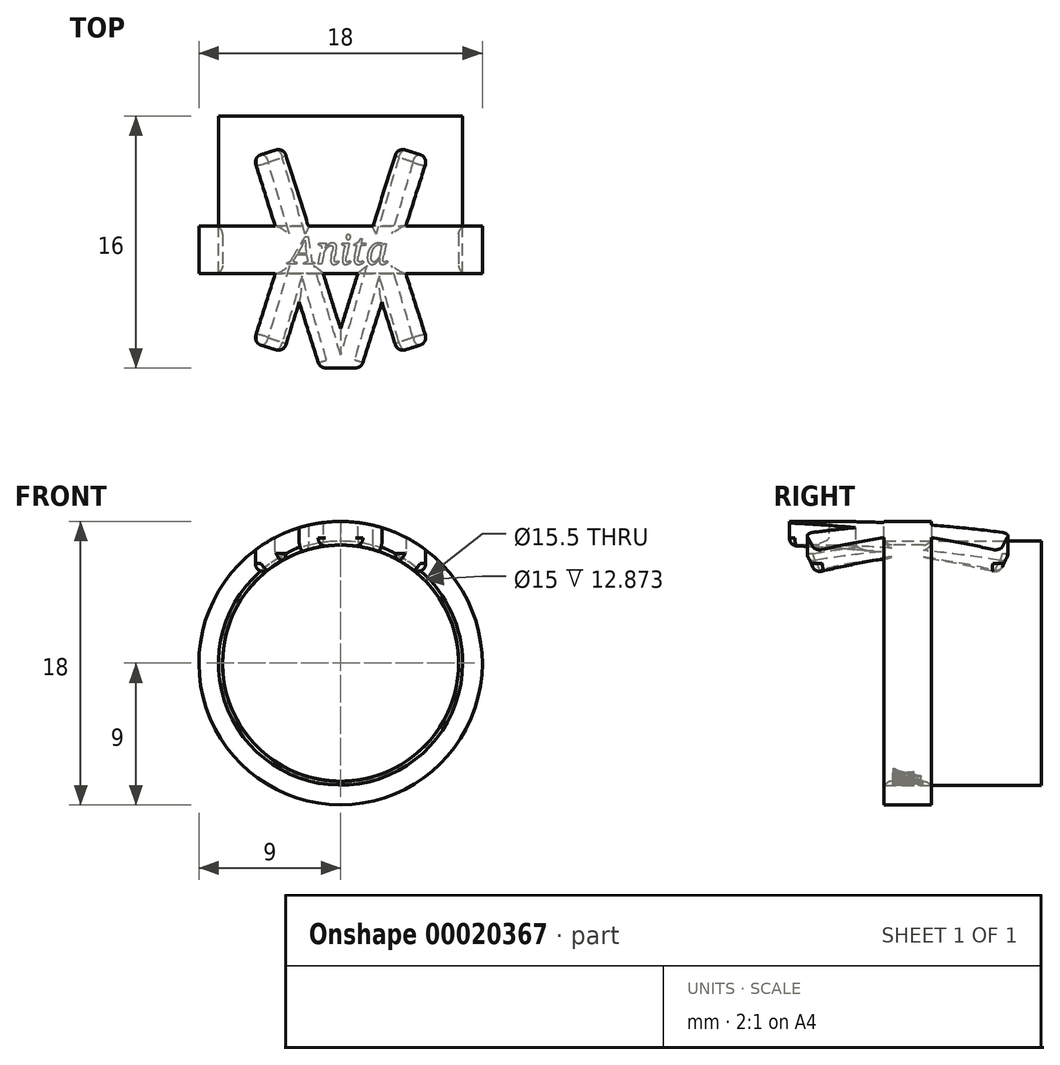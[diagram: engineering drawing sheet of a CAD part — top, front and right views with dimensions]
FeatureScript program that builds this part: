
annotation { "Feature Type Name" : "Feature", "Feature Type Description" : "" }
export const myFeature = defineFeature(function(context is Context, id is Id, definition is map)
    precondition{}
    {
        {
            var Q0;
            Q0=qCreatedBy(makeId("Right.planeOp"),FACE);
            var sketch = newSketch(context, id + "F0", { "sketchPlane" : qUnion([Q0])});
            skLineSegment(sketch, "E0.bottom", {"start": v(-1.5, 9) * mm, "end": v(1.5, 9) * mm});
            skLineSegment(sketch, "E0.top", {"start": v(-1.5, 7.5) * mm, "end": v(1.5, 7.5) * mm});
            skLineSegment(sketch, "E0.left", {"start": v(-1.5, 9) * mm, "end": v(-1.5, 7.5) * mm});
            skLineSegment(sketch, "E0.right", {"start": v(1.5, 9) * mm, "end": v(1.5, 7.5) * mm});
            skLineSegment(sketch, "E1", {"start": v(0, 0) * mm, "end": v(0, 30.06) * mm, "construction": true});
            skLineSegment(sketch, "E2", {"start": v(-13.24, 0) * mm, "end": v(16.31, 0) * mm, "construction": true});
            skSolve(sketch);
        }
        {
            var Q0;
            Q0=makeQuery(id+"F0.imprint","IMPRINT",FACE,{"disambiguationData":[TD([[makeQuery(id+"F0.imprint","IMPRINT",EDGE,{"derivedFrom":sQuery(id+"F0.wireOp",EDGE,"E0.bottom")}),-1.0]])]});
            var Q1;
            Q1=sQuery(id+"F0.wireOp",EDGE,"E2");
            revolve(context, id + "F1", {"entities" : qUnion([Q0]), "axis" : qUnion([Q1]), "revolveType" : RevolveType.FULL});
        }
        {
            var Q0;
            Q0=qCreatedBy(makeId("Top.planeOp"),FACE);
            var sketch = newSketch(context, id + "F2", { "sketchPlane" : qUnion([Q0])});
            skLineSegment(sketch, "E3", {"start": v(0, 6.73) * mm, "end": v(0, -7.13) * mm, "construction": true});
            skLineSegment(sketch, "E4", {"start": v(-3.63, -6.5) * mm, "end": v(0, 5) * mm});
            skLineSegment(sketch, "E5", {"start": v(0, 5) * mm, "end": v(3.63, -6.5) * mm});
            skLineSegment(sketch, "E6", {"start": v(-3.63, -6.5) * mm, "end": v(-5.53, -5.9) * mm});
            skLineSegment(sketch, "E7", {"start": v(-5.53, -5.9) * mm, "end": v(-1.3, 7.5) * mm});
            skLineSegment(sketch, "E8", {"start": v(-1.3, 7.5) * mm, "end": v(1.3, 7.5) * mm});
            skLineSegment(sketch, "E9", {"start": v(1.3, 7.5) * mm, "end": v(5.53, -5.9) * mm});
            skLineSegment(sketch, "E10", {"start": v(3.63, -6.5) * mm, "end": v(5.53, -5.9) * mm});
            skLineSegment(sketch, "E11", {"start": v(-10.55, 0) * mm, "end": v(12.02, 0) * mm, "construction": true});
            skLineSegment(sketch, "E12.MirrorCS", {"start": v(3.63, 6.5) * mm, "end": v(5.53, 5.9) * mm});
            skLineSegment(sketch, "E13.MirrorCS", {"start": v(-3.63, 6.5) * mm, "end": v(-5.53, 5.9) * mm});
            skLineSegment(sketch, "E14.MirrorCS", {"start": v(-5.53, 5.9) * mm, "end": v(-1.3, -7.5) * mm});
            skLineSegment(sketch, "E15.MirrorCS", {"start": v(-3.63, 6.5) * mm, "end": v(0, -5) * mm});
            skLineSegment(sketch, "E16.MirrorCS", {"start": v(0, -5) * mm, "end": v(3.63, 6.5) * mm});
            skLineSegment(sketch, "E17.MirrorCS", {"start": v(-1.3, -7.5) * mm, "end": v(1.3, -7.5) * mm});
            skLineSegment(sketch, "E18.MirrorCS", {"start": v(1.3, -7.5) * mm, "end": v(5.53, 5.9) * mm});
            skSolve(sketch);
        }
        {
            var Q0;
            Q0=makeQuery(id+"F1.opRevolve","SWEPT_FACE",FACE,{"disambiguationData":[OSD([sQuery(id+"F0.wireOp",EDGE,"E0.left")])]});
            var sketch = newSketch(context, id + "F3", { "sketchPlane" : qUnion([Q0])});
            skCircle(sketch, "E19.0", {"center": v(0, 0) * mm, "radius": 7.5 * mm});
            skCircle(sketch, "E20.0", {"center": v(0, 0) * mm, "radius": 9 * mm});
            skSolve(sketch);
        }
        {
            var Q0;
            {var subQ3=sQuery(id+"F2.wireOp",EDGE,"E13.MirrorCS");Q0=makeQuery(id+"F2.imprint","IMPRINT",FACE,{"disambiguationData":[TD([[makeQuery(id+"F2.imprint","IMPRINT",EDGE,{"derivedFrom":subQ3}),1.0]])]});}
            var Q1;
            {var subQ1=sQuery(id+"F2.wireOp",EDGE,"E4");var subQ5=sQuery(id+"F2.wireOp",EDGE,"E14.MirrorCS");var subQ7=makeQuery(id+"F2.imprint","INTERSECT",VERTEX,{"derivedFrom":[subQ1,subQ5]});Q1=makeQuery(id+"F2.imprint","IMPRINT",FACE,{"disambiguationData":[TD([[makeQuery(id+"F2.imprint","IMPRINT",EDGE,{"disambiguationData":[TD([[subQ7,-1.0]])],"derivedFrom":subQ1}),1.0]])]});}
            var Q2;
            {var subQ5=sQuery(id+"F2.wireOp",EDGE,"E6");Q2=makeQuery(id+"F2.imprint","IMPRINT",FACE,{"disambiguationData":[TD([[makeQuery(id+"F2.imprint","IMPRINT",EDGE,{"derivedFrom":subQ5}),-1.0]])]});}
            var Q3;
            {var subQ3=sQuery(id+"F2.wireOp",EDGE,"E17.MirrorCS");Q3=makeQuery(id+"F2.imprint","IMPRINT",FACE,{"disambiguationData":[TD([[makeQuery(id+"F2.imprint","IMPRINT",EDGE,{"derivedFrom":subQ3}),1.0]])]});}
            var Q4;
            {var subQ5=sQuery(id+"F2.wireOp",EDGE,"E10");Q4=makeQuery(id+"F2.imprint","IMPRINT",FACE,{"disambiguationData":[TD([[makeQuery(id+"F2.imprint","IMPRINT",EDGE,{"derivedFrom":subQ5}),1.0]])]});}
            var Q5;
            {var subQ3=sQuery(id+"F2.wireOp",EDGE,"E12.MirrorCS");Q5=makeQuery(id+"F2.imprint","IMPRINT",FACE,{"disambiguationData":[TD([[makeQuery(id+"F2.imprint","IMPRINT",EDGE,{"derivedFrom":subQ3}),-1.0]])]});}
            var Q6;
            {var subQ0=sQuery(id+"F2.wireOp",EDGE,"E18.MirrorCS");var subQ3=sQuery(id+"F2.wireOp",EDGE,"E5");var subQ4=makeQuery(id+"F2.imprint","INTERSECT",VERTEX,{"derivedFrom":[subQ3,subQ0]});Q6=makeQuery(id+"F2.imprint","IMPRINT",FACE,{"disambiguationData":[TD([[makeQuery(id+"F2.imprint","IMPRINT",EDGE,{"disambiguationData":[TD([[subQ4,1.0]])],"derivedFrom":subQ3}),1.0]])]});}
            var Q7;
            {var subQ10=sQuery(id+"F2.wireOp",EDGE,"E8");Q7=makeQuery(id+"F2.imprint","IMPRINT",FACE,{"disambiguationData":[TD([[makeQuery(id+"F2.imprint","IMPRINT",EDGE,{"derivedFrom":subQ10}),-1.0]])]});}
            var Q8;
            Q8=makeQuery(id+"F1.opRevolve","SWEPT_FACE",FACE,{"disambiguationData":[OSD([sQuery(id+"F0.wireOp",EDGE,"E0.bottom")])]});
            extrude(context, id + "F4", {"entities" : qUnion([Q0, Q1, Q2, Q3, Q4, Q5, Q6, Q7]), "operationType" : NewBodyOperationType.ADD, "endBound" : BoundingType.UP_TO_SURFACE, "endBoundEntityFace" : qUnion([Q8]), "depth" : 25 * mm});
        }
        {
            var Q0;
            Q0=makeQuery(id+"F3.imprint","IMPRINT",FACE,{"disambiguationData":[TD([[makeQuery(id+"F3.imprint","IMPRINT",EDGE,{"derivedFrom":sQuery(id+"F3.wireOp",EDGE,"E19.0")}),1.0]])]});
            extrude(context, id + "F5", {"entities" : qUnion([Q0]), "operationType" : NewBodyOperationType.REMOVE, "oppositeDirection" : true, "depth" : 25 * mm, "symmetric" : true});
        }
        {
            var Q0;
            Q0=makeQuery(id+"F4.opExtrude","SWEPT_EDGE",EDGE,{"disambiguationData":[OSD([sQuery(id+"F2.wireOp",EDGE,"E12.MirrorCS"),sQuery(id+"F2.wireOp",EDGE,"E18.MirrorCS")])]});
            var Q1;
            Q1=makeQuery(id+"F4.opExtrude","SWEPT_EDGE",EDGE,{"disambiguationData":[OSD([sQuery(id+"F2.wireOp",EDGE,"E12.MirrorCS"),sQuery(id+"F2.wireOp",EDGE,"E16.MirrorCS")])]});
            var Q2;
            Q2=makeQuery(id+"F4.opExtrude","SWEPT_EDGE",EDGE,{"disambiguationData":[OSD([sQuery(id+"F2.wireOp",EDGE,"E8"),sQuery(id+"F2.wireOp",EDGE,"E9")])]});
            var Q3;
            Q3=makeQuery(id+"F4.opExtrude","SWEPT_EDGE",EDGE,{"disambiguationData":[OSD([sQuery(id+"F2.wireOp",EDGE,"E7"),sQuery(id+"F2.wireOp",EDGE,"E8")])]});
            var Q4;
            Q4=makeQuery(id+"F4.opExtrude","SWEPT_EDGE",EDGE,{"disambiguationData":[OSD([sQuery(id+"F2.wireOp",EDGE,"E13.MirrorCS"),sQuery(id+"F2.wireOp",EDGE,"E15.MirrorCS")])]});
            var Q5;
            Q5=makeQuery(id+"F4.opExtrude","SWEPT_EDGE",EDGE,{"disambiguationData":[OSD([sQuery(id+"F2.wireOp",EDGE,"E13.MirrorCS"),sQuery(id+"F2.wireOp",EDGE,"E14.MirrorCS")])]});
            var Q6;
            Q6=makeQuery(id+"F4.opExtrude","SWEPT_EDGE",EDGE,{"disambiguationData":[OSD([sQuery(id+"F2.wireOp",EDGE,"E6"),sQuery(id+"F2.wireOp",EDGE,"E7")])]});
            var Q7;
            Q7=makeQuery(id+"F4.opExtrude","SWEPT_EDGE",EDGE,{"disambiguationData":[OSD([sQuery(id+"F2.wireOp",EDGE,"E4"),sQuery(id+"F2.wireOp",EDGE,"E6")])]});
            var Q8;
            Q8=makeQuery(id+"F4.opExtrude","SWEPT_EDGE",EDGE,{"disambiguationData":[OSD([sQuery(id+"F2.wireOp",EDGE,"E14.MirrorCS"),sQuery(id+"F2.wireOp",EDGE,"E17.MirrorCS")])]});
            var Q9;
            Q9=makeQuery(id+"F4.opExtrude","SWEPT_EDGE",EDGE,{"disambiguationData":[OSD([sQuery(id+"F2.wireOp",EDGE,"E17.MirrorCS"),sQuery(id+"F2.wireOp",EDGE,"E18.MirrorCS")])]});
            var Q10;
            Q10=makeQuery(id+"F4.opExtrude","SWEPT_EDGE",EDGE,{"disambiguationData":[OSD([sQuery(id+"F2.wireOp",EDGE,"E5"),sQuery(id+"F2.wireOp",EDGE,"E10")])]});
            var Q11;
            Q11=makeQuery(id+"F4.opExtrude","SWEPT_EDGE",EDGE,{"disambiguationData":[OSD([sQuery(id+"F2.wireOp",EDGE,"E9"),sQuery(id+"F2.wireOp",EDGE,"E10")])]});
            fillet(context, id + "F6", {"entities" : qUnion([Q0, Q1, Q2, Q3, Q4, Q5, Q6, Q7, Q8, Q9, Q10, Q11]), "radius" : .5 * mm, "tangentPropagation" : true, "allowEdgeOverflow" : false});
        }
        {
            var Q0;
            {var subQ0=makeQuery(id+"F1.opRevolve","SWEPT_FACE",FACE,{"disambiguationData":[OSD([sQuery(id+"F0.wireOp",EDGE,"E0.top")])]});var subQ2=sQuery(id+"F2.wireOp",EDGE,"E5");var subQ6=sQuery(id+"F2.wireOp",EDGE,"E4");var subQ8=makeQuery(id+"F2.imprint","INTERSECT",VERTEX,{"derivedFrom":[subQ6,subQ2]});var subQ15=sQuery(id+"F2.wireOp",EDGE,"E7");Q0=makeQuery(id+"F5.boolean.opBoolean","MERGE",FACE,{"derivedFrom":[makeQuery(id+"F4.boolean.opBoolean","SPLIT",FACE,{"disambiguationData":[TD([makeQuery(id+"F4.opExtrude","SWEPT_FACE",FACE,{"disambiguationData":[OSD([subQ6]),TDD([makeQuery(id+"F2.imprint","IMPRINT",EDGE,{"disambiguationData":[TD([[subQ8,1.0]])],"derivedFrom":subQ6})])]})])],"derivedFrom":subQ0}),makeQuery(id+"F4.boolean.opBoolean","SPLIT",FACE,{"disambiguationData":[TD([makeQuery(id+"F4.opExtrude","SWEPT_FACE",FACE,{"disambiguationData":[OSD([subQ15]),TDD([makeQuery(id+"F2.imprint","IMPRINT",EDGE,{"disambiguationData":[TD([[makeQuery(id+"F2.imprint","INTERSECT",VERTEX,{"derivedFrom":[sQuery(id+"F2.wireOp",EDGE,"E6"),subQ15]}),-1.0]])],"derivedFrom":subQ15})])]})])],"derivedFrom":subQ0}),makeQuery(id+"F5.opExtrude","SWEPT_FACE",FACE,{"disambiguationData":[OSD([sQuery(id+"F3.wireOp",EDGE,"E19.0")])]})]});}
            fillet(context, id + "F7", {"entities" : qUnion([Q0]), "radius" : .5 * mm, "tangentPropagation" : true, "allowEdgeOverflow" : false});
        }
        {
            var Q0;
            Q0=qCreatedBy(makeId("Top.planeOp"),FACE);
            var sketch = newSketch(context, id + "F8", { "sketchPlane" : qUnion([Q0])});
            skText(sketch, "E21", { "text": "Anita", "fontName": "NotoSerif-Italic.ttf"});
            const initialGuessF8  = {"E21": [-0.00327, -0.0009, 1, 0, 0.00177]};
            skSetInitialGuess(sketch, initialGuessF8);
            skSolve(sketch);
        }
        {
            var Q0;
            {var subQ3=sQuery(id+"F2.wireOp",EDGE,"E7");var subQ5=sQuery(id+"F2.wireOp",EDGE,"E6");Q0=makeQuery(id+"F4.boolean.opBoolean","SPLIT",FACE,{"disambiguationData":[TD([makeQuery(id+"F4.opExtrude","SWEPT_FACE",FACE,{"disambiguationData":[OSD([subQ3]),TDD([makeQuery(id+"F2.imprint","IMPRINT",EDGE,{"disambiguationData":[TD([[makeQuery(id+"F2.imprint","INTERSECT",VERTEX,{"derivedFrom":[subQ5,subQ3]}),-1.0]])],"derivedFrom":subQ3})])]})])],"derivedFrom":makeQuery(id+"F1.opRevolve","SWEPT_FACE",FACE,{"disambiguationData":[OSD([sQuery(id+"F0.wireOp",EDGE,"E0.left")])]})});}
            var sketch = newSketch(context, id + "F9", { "sketchPlane" : qUnion([Q0])});
            skCircle(sketch, "E22", {"center": v(0, 0) * mm, "radius": 7.75 * mm});
            skSolve(sketch);
        }
        {
            var Q0;
            {var subQ0=sQuery(id+"F9.wireOp",EDGE,"E22");Q0=makeQuery(id+"F9.imprint","IMPRINT",FACE,{"disambiguationData":[TD([[makeQuery(id+"F9.imprint","IMPRINT",EDGE,{"disambiguationData":[OD(0.0)],"derivedFrom":subQ0}),-1.0]])]});}
            var Q1;
            Q1=sQuery(id+"F9.wireOp",EDGE,"E22");
            extrude(context, id + "F10", {"entities" : qUnion([Q0]), "bodyType" : ExtendedToolBodyType.SURFACE, "surfaceEntities" : qUnion([Q1]), "oppositeDirection" : true, "depth" : 10 * mm});
        }
        {
            var Q0;
            Q0 = qSketchRegion(id + "F8", true);
            var Q1;
            Q1=makeQuery(id+"F10.opExtrude","SWEPT_FACE",FACE,{"disambiguationData":[OSD([sQuery(id+"F9.wireOp",EDGE,"E22")])]});
            extrude(context, id + "F11", {"entities" : qUnion([Q0]), "operationType" : NewBodyOperationType.REMOVE, "endBound" : BoundingType.UP_TO_SURFACE, "oppositeDirection" : true, "endBoundEntityFace" : qUnion([Q1]), "depth" : 25 * mm});
        }
    });
